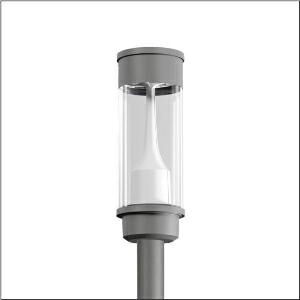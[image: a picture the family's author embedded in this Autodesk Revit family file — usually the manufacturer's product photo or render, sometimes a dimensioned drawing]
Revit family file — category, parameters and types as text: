
# Revit family: litepole_iq___pl1_2s_5xa5415rf14h_7319
name_source: partatom
category: Lighting Fixtures
units: mm (PartAtom-declared; Revit-internal decimal feet)

## family parameters
Cut with Voids When Loaded = No
Host = Face
Light Source = No
Part Type = Normal
Room Calculation Point = No
Round Connector Dimension = Use Diameter
Shared = No

## types (1)
- --- (1 x LED, 2970 lm, 18.5 W, 4000K)
    Apparent Load = 19 VA
    CIE Flux Codes = 23 62 94 96 100
    Color Rendering = 70
    Color Temperature = 4000K
    Default Elevation = 1800 mm
    Description = Litepole iQ, mast luminaire, Module 540 iQ-SR, primary light control with 3 zone facetted reflector, of plastic, silver coated, highly specular, structured, primary optical cover: cover, of PMMA, transparent, light distribution: PL1.2s, light emission: direct distribution, primary light characteristic: symmetric, installation type: post-top, LED, High Power LED, rated luminous flux: 2.970lm, luminous efficacy: 161lm/W, light colour: 740, colour temperature: 4000K, control gear: ECG iQ, control: optimised constant luminous flux control (CLO 2.0), Desk-Remote (wireless, voltage-free reading and setting of iQ features in the workshop via application-optimized NFC function/RFID function), Light-Fading, Smart-Wire, Night-Set, Lumen-Switch, Temp-Guard, Auto-Match, Street-Remote, presetting dimming logarithmic, with terminal, 6-pole, max. 2.5mm², mains connection: 230..240V, AC, 50/60Hz, start of lifetime: 19W, end of service life: 20W, reduction: 9W, luminaire housing, upper part, of glass-fibre reinforced polyester, coated, Siteco® metallic grey (DB 702S), diameter: 210mm, height: 590mm, spigot size: d x l = 76 x 70mm (post-top) | with reducer (optional accessory) 60 x 70mm, post-top mast mounting element, of diecast aluminium, coated, Siteco® metallic grey (DB 702S), Module 540 iQ-SR, traffic white (RAL 9016), equipment: standard, protection rating (complete): IP65, insulation class (complete): insulation class II (safety insulation), certification: CE, ENEC, VDE, packaging unit: 1 piece

Light Distribution: PL1.2s
    Height = 590 mm
    Lamp = 1 x LED
    Lamp Light Flux = 2970 lm
    Lamp Power = 18.5 W
    Lamp count = 1
    Length = 220 mm
    Luminous efficacy = 161 lm/W
    Manufacturer = Siteco
    ModVariant = No
    Model = 5XA5415RF14H
    Number of Poles = 1
    OnlyDefault = Yes
    Power Factor = 1
    Product Name = Litepole iQ | PL1.2s
    Product group = mast luminaire | pylon top
    ProductGroupID = 6100
    Protection Class = Protection class II
    Protection Degree = IP 65
    RLX_Detail_Level = 1
    RLX_Emergency_Light_Flux = 0 lm
    RLX_Emergency_Type = 0
    RLX_Emergency_Type_DB = No
    RlxData = <blob elided: 40325 chars, md5=75d9da04>
    Socket = socket
    Standby Power = 0 W
    System Light Flux = 2970 lm
    System Power = 19 W
    Type Comments = factory setting: luminous flux: 100 % | dim-lin: 254 | 385 mA
    Type Image = l_1006025.jpg
    URL = http://relux.com
    VarID = @adj_094287
    Voltage = 0 V
    Weight = 0.00 kg
    Width = 0 mm  [stored 0 ft]

note: [stored X ft] marks values corroborated as IEEE doubles in the binary element streams (Revit-internal decimal feet)

## geometry (parser evidence)
native form markers: Blend x4, Sweep x10
no freeform markers — native parametric forms only
